# Revit family: 45720CHN_new
name_source: partatom
category: Furniture
revit_build: Autodesk Revit 2018 (Build: 20170223_1515(x64)
units: mm (PartAtom-declared; Revit-internal decimal feet)

## family parameters
Always vertical = No
Cut with Voids When Loaded = No
OmniClass Number = 23.40.20.00
OmniClass Title = General Furniture and Specialties
Room Calculation Point = No
Shared = No
Work Plane-Based = No

## types (3) — shared parameters
Always visible = Yes
BIMobject category = Other Sanitary
Design country = Germany
EAN code = 4059625032824
Edition number = 1
IFC Classification = Sanitary Terminal
Installation instructions = https://www.axor-design.com
Manufacturer country = Germany
Manufacturer name = AXOR
Material main = Chrome
Product Guid = ef38e70e-fcfa-46c1-afa7-68bfd2947c45
Product SKU = 45720CHN
Product data url = https://www.bimobject.com
Product family = AXOR One
Product group = Hand showers
Product name = 45720CHN AXOR One Hand shower 2jet
Product url = https://www.axor-design.com
QR code = https://www.bimobject.com
Technical description = https://www.axor-design.com

## per-type parameters (varying)
| type | Material 1 |
| 997 Polished Gold Optic | AXOR - AXOR One - 997 Polished Gold Optic |
| 347 Brushed Black Chrome | AXOR - AXOR One - 347 Brushed Black Chrome |
| 007 Chrome | AXOR - AXOR One - 007 Chrome |

## geometry (parser evidence)
native form markers: Sweep x2
no freeform markers — native parametric forms only
